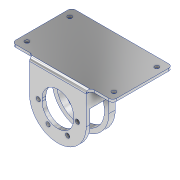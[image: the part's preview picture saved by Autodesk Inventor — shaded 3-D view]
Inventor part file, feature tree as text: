
AUTODESK INVENTOR PART (.ipt)
format: ipt  version: 2022 (Build 260153000, 153)  size: 276,992 bytes
history: native  units: mm
features: sketch x8, extrude x5, sheet_metal_op x2, hole x2, thicken_offset x1, fillet x1, plane x1, mirror x1, other x1, projected_geometry x1
ambient origin geometry x8: Origin, YZ Plane, XZ Plane, XY Plane, X Axis, Y Axis, Z Axis, Center Point
bodies: Solid1 (feature_tree)
feature tree (23):
  extrude  "Extrusion1"  Depth=6.5mm
  sheet_metal_op  "Face1"
  extrude  "Extrusion3"  Depth=45.0mm
  hole  "Hole1"  [1 undecoded]
  hole  "Hole2"  [1 undecoded]
  extrude  "Extrusion2"  Depth=2.0mm
  thicken_offset  "Thicken2"
  fillet  "Fillet2"  Radius=31.0mm
  plane  "Work Plane1"
  extrude  "Extrusion4"  Depth=20.594885mm
  extrude  "Extrusion5"  Depth=3.0mm
  mirror  "Mirror2"
  sketch  "Sketch1"  dims[d1=37.0mm d3=6.5mm]
  sketch  "Sketch2"  dims[d4=50.0mm d5=45.0mm]
  other  "Plate1"
  sheet_metal_op  "Bend1"
  sketch  "Sketch3"  dims[d6=2.0mm d7=0.0mm d8=2.0mm]
  sketch  "Sketch4"  dims[d9=0.5mm d10=2.0mm d11=1.0mm]
  sketch  "Sketch6"  dims[d12=4.0mm d13=2.0mm d14=31.0mm]
  sketch  "Sketch8"  dims[d15=30.0mm d17=360.0deg]
  sketch  "Sketch10"  dims[d19=3.4mm d20=6.0mm d21=4.0mm d22=2.0mm d23=90.0deg d24=2.0mm d25=20.594885mm]
  sketch  "Sketch12"  dims[d26=34.0mm d27=69.0mm d28=3.4mm d29=6.0mm d30=4.0mm d31=2.0mm d32=90.0deg d33=8.0mm d34=20.594885mm d36=7.0mm d45=25.0mm d46=2.0mm d47=0.0mm d48=0.0mm d50=80.0mm d51=10.0mm d52=0.0mm d53=3.0mm d56=1.0mm d57=1.0mm d66=-18.0mm d69=38.0mm d70=5.0mm d71=0.0mm d72=12.0mm d73=14.0mm d74=3.0mm d75=0.0mm]
  projected_geometry  "Project Cut Edges1"
note: 2 required parameter values undecoded (feature->parameter linkage not recoverable at this tier; creation-order binding heuristic only, values carry confidence <= 0.55)
